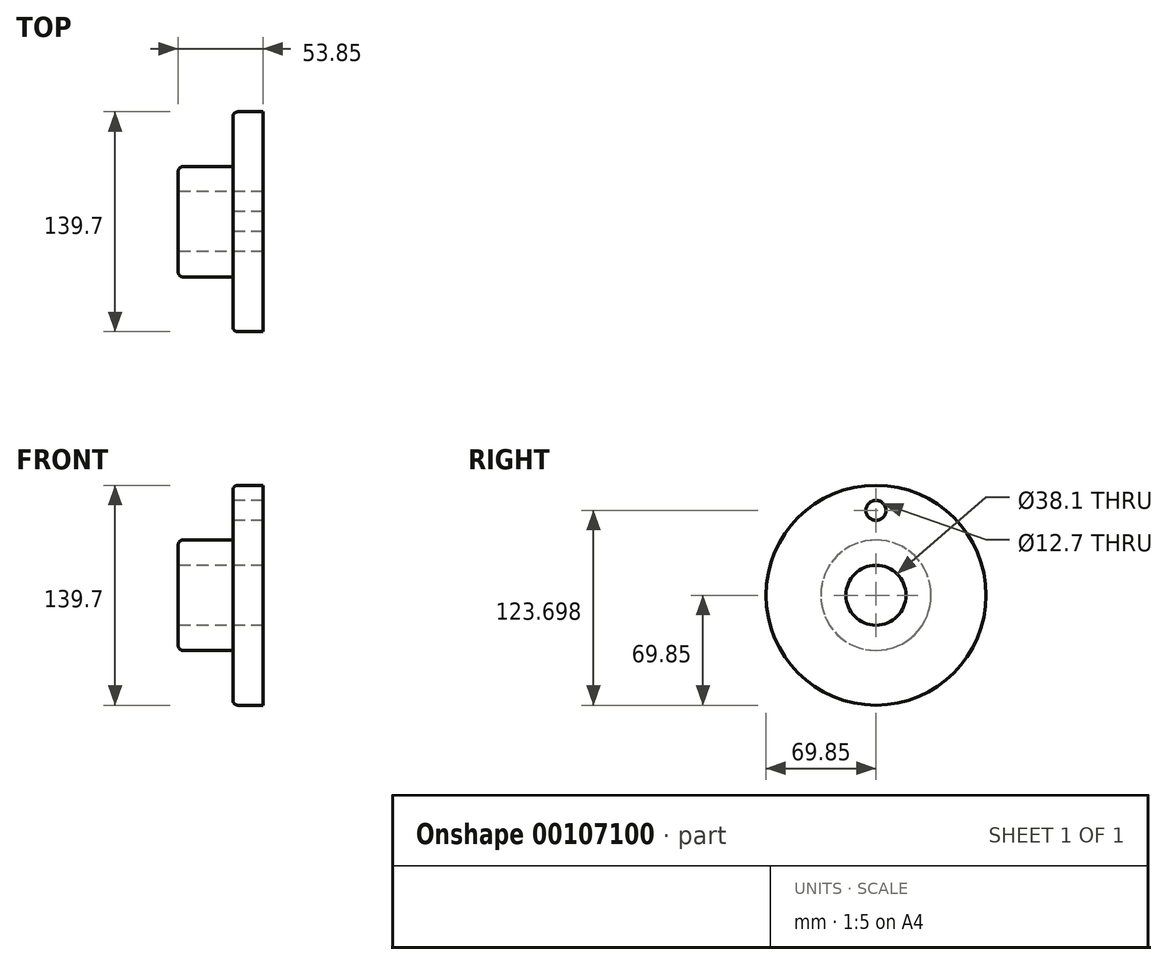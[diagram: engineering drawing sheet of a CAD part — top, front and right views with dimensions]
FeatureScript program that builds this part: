
annotation { "Feature Type Name" : "Feature", "Feature Type Description" : "" }
export const myFeature = defineFeature(function(context is Context, id is Id, definition is map)
    precondition{}
    {
        {
            var Q0;
            Q0=qCreatedBy(makeId("Front.planeOp"),FACE);
            var sketch = newSketch(context, id + "F0", { "sketchPlane" : qUnion([Q0])});
            skLineSegment(sketch, "E0", {"start": v(0, 0) * mm, "end": v(53.85, 0) * mm, "construction": true});
            skLineSegment(sketch, "E1", {"start": v(0, 19.05) * mm, "end": v(53.85, 19.05) * mm});
            skLineSegment(sketch, "E2", {"start": v(53.85, 19.05) * mm, "end": v(53.85, 69.85) * mm});
            skLineSegment(sketch, "E3", {"start": v(53.85, 69.85) * mm, "end": v(34.8, 69.85) * mm});
            skLineSegment(sketch, "E4", {"start": v(34.8, 69.85) * mm, "end": v(34.8, 35.05) * mm});
            skLineSegment(sketch, "E5", {"start": v(34.8, 35.05) * mm, "end": v(0, 35.05) * mm});
            skLineSegment(sketch, "E6", {"start": v(0, 35.05) * mm, "end": v(0, 19.05) * mm});
            skSolve(sketch);
        }
        {
            var Q0;
            Q0=makeQuery(id+"F0.imprint","IMPRINT",FACE,{"disambiguationData":[TD([[makeQuery(id+"F0.imprint","IMPRINT",EDGE,{"derivedFrom":sQuery(id+"F0.wireOp",EDGE,"E1")}),1.0]])]});
            var Q1;
            Q1=sQuery(id+"F0.wireOp",EDGE,"E0");
            revolve(context, id + "F1", {"entities" : qUnion([Q0]), "axis" : qUnion([Q1]), "revolveType" : RevolveType.FULL});
        }
        {
            var Q0;
            Q0=makeQuery(id+"F1.opRevolve","SWEPT_FACE",FACE,{"disambiguationData":[OSD([sQuery(id+"F0.wireOp",EDGE,"E4")])]});
            var sketch = newSketch(context, id + "F2", { "sketchPlane" : qUnion([Q0])});
            skCircle(sketch, "E7", {"center": v(0, 53.85) * mm, "radius": 6.35 * mm});
            skSolve(sketch);
        }
        {
            var Q0;
            Q0=makeQuery(id+"F2.imprint","IMPRINT",FACE,{"disambiguationData":[TD([[makeQuery(id+"F2.imprint","IMPRINT",EDGE,{"derivedFrom":sQuery(id+"F2.wireOp",EDGE,"E7")}),1.0]])]});
            extrude(context, id + "F3", {"entities" : qUnion([Q0]), "operationType" : NewBodyOperationType.REMOVE, "endBound" : BoundingType.THROUGH_ALL, "oppositeDirection" : true, "depth" : 25.4 * mm});
        }
        {
            var Q0;
            Q0=makeQuery(id+"F1.opRevolve","SWEPT_EDGE",EDGE,{"disambiguationData":[OSD([sQuery(id+"F0.wireOp",EDGE,"E5"),sQuery(id+"F0.wireOp",EDGE,"E6")])]});
            var Q1;
            Q1=makeQuery(id+"F1.opRevolve","SWEPT_EDGE",EDGE,{"disambiguationData":[OSD([sQuery(id+"F0.wireOp",EDGE,"E3"),sQuery(id+"F0.wireOp",EDGE,"E4")])]});
            fillet(context, id + "F4", {"entities" : qUnion([Q0, Q1]), "radius" : 3.05 * mm, "tangentPropagation" : true, "allowEdgeOverflow" : false});
        }
    });
